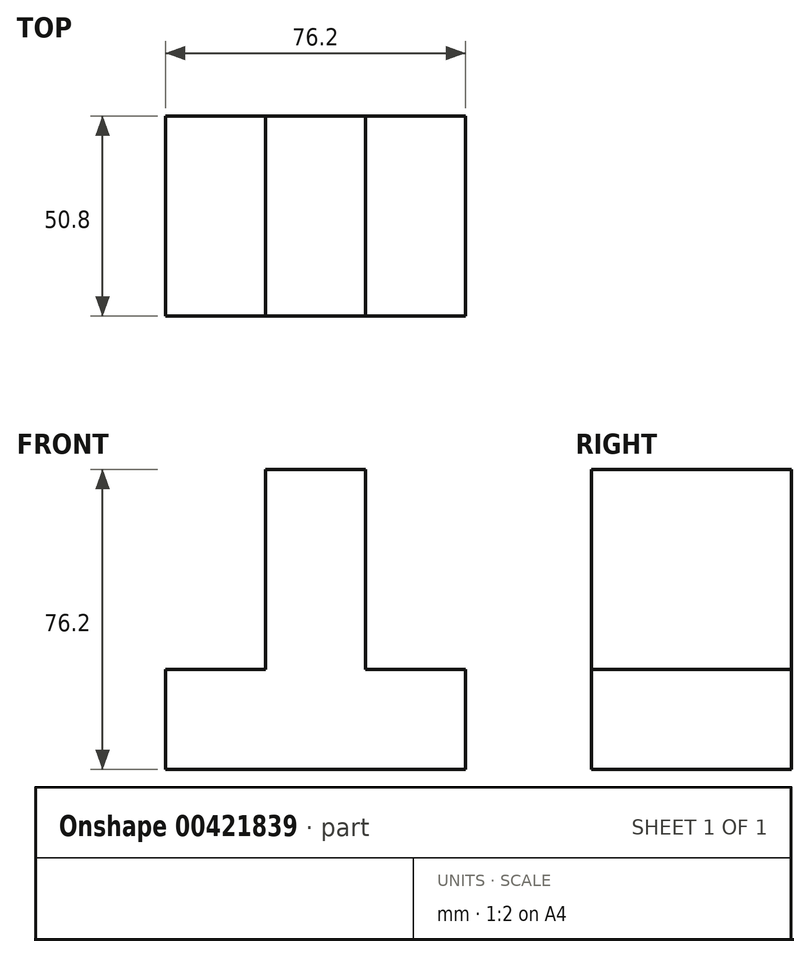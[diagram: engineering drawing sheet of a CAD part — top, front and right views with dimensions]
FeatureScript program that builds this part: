
annotation { "Feature Type Name" : "Feature", "Feature Type Description" : "" }
export const myFeature = defineFeature(function(context is Context, id is Id, definition is map)
    precondition{}
    {
        {
            var Q0;
            Q0=qCreatedBy(makeId("Front.planeOp"),FACE);
            var sketch = newSketch(context, id + "F0", { "sketchPlane" : qUnion([Q0])});
            skLineSegment(sketch, "E0", {"start": v(0, 0) * mm, "end": v(76.2, 0) * mm});
            skLineSegment(sketch, "E1", {"start": v(0, 0) * mm, "end": v(0, 25.4) * mm});
            skLineSegment(sketch, "E2", {"start": v(0, 25.4) * mm, "end": v(25.4, 25.4) * mm});
            skLineSegment(sketch, "E3", {"start": v(25.4, 25.4) * mm, "end": v(25.4, 76.2) * mm});
            skLineSegment(sketch, "E4", {"start": v(76.2, 0) * mm, "end": v(76.2, 25.4) * mm});
            skLineSegment(sketch, "E5", {"start": v(76.2, 25.4) * mm, "end": v(50.8, 25.4) * mm});
            skLineSegment(sketch, "E6", {"start": v(50.8, 25.4) * mm, "end": v(50.8, 76.2) * mm});
            skLineSegment(sketch, "E7", {"start": v(50.8, 76.2) * mm, "end": v(25.4, 76.2) * mm});
            skSolve(sketch);
        }
        {
            var Q0;
            Q0=makeQuery(id+"F0.imprint","IMPRINT",FACE,{"disambiguationData":[TD([[makeQuery(id+"F0.imprint","IMPRINT",EDGE,{"derivedFrom":sQuery(id+"F0.wireOp",EDGE,"E0")}),1.0]])]});
            extrude(context, id + "F1", {"entities" : qUnion([Q0]), "depth" : 50.8 * mm});
        }
    });
